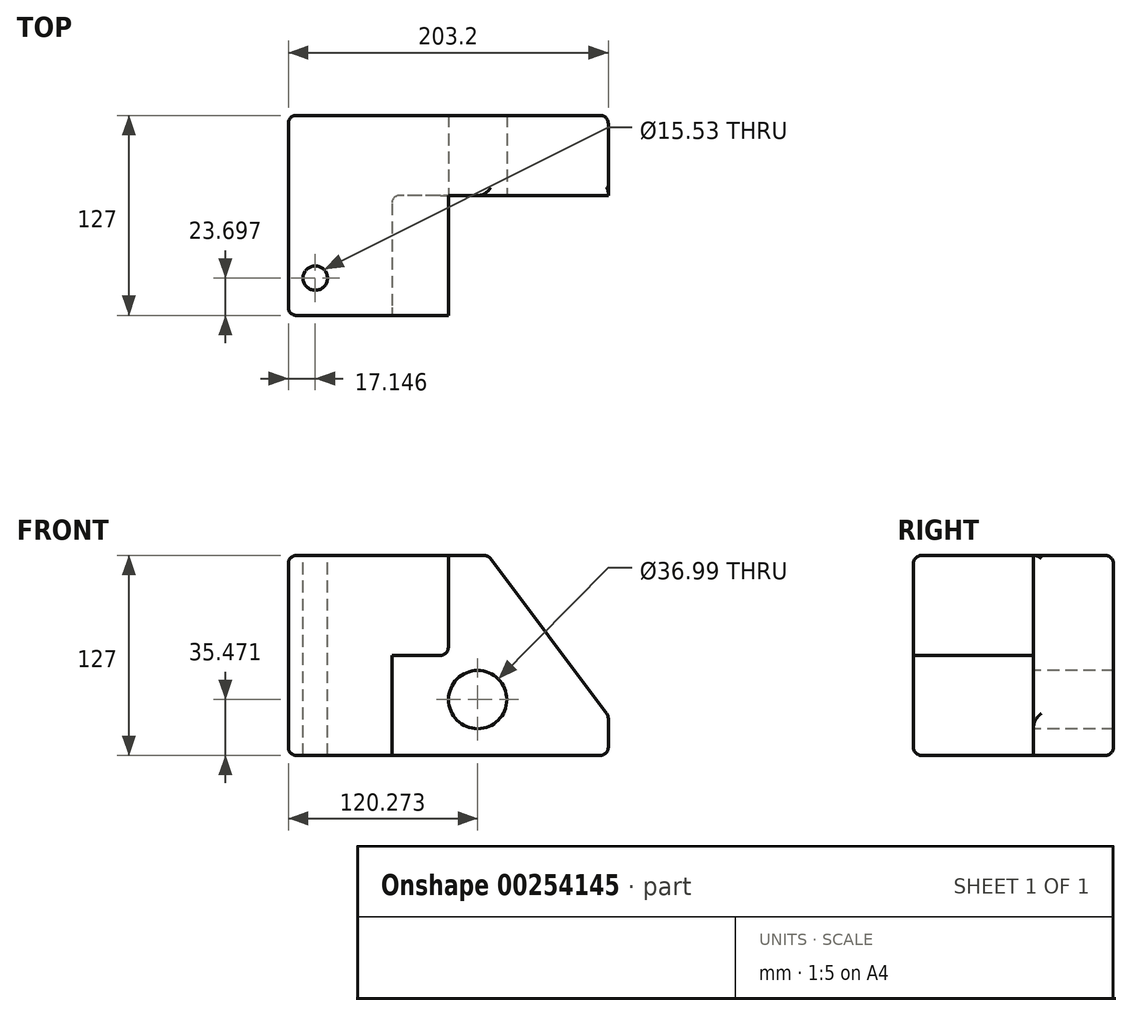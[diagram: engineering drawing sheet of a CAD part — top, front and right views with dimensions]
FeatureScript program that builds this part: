
annotation { "Feature Type Name" : "Feature", "Feature Type Description" : "" }
export const myFeature = defineFeature(function(context is Context, id is Id, definition is map)
    precondition{}
    {
        {
            var Q0;
            Q0=qCreatedBy(makeId("Front.planeOp"),FACE);
            var sketch = newSketch(context, id + "F0", { "sketchPlane" : qUnion([Q0])});
            skLineSegment(sketch, "E0.bottom", {"start": v(101.6, -63.5) * mm, "end": v(-101.6, -63.5) * mm});
            skLineSegment(sketch, "E0.top", {"start": v(101.6, 63.5) * mm, "end": v(-101.6, 63.5) * mm});
            skLineSegment(sketch, "E0.left", {"start": v(101.6, -63.5) * mm, "end": v(101.6, 63.5) * mm});
            skLineSegment(sketch, "E0.right", {"start": v(-101.6, -63.5) * mm, "end": v(-101.6, 63.5) * mm});
            skPoint(sketch, "E0.middle", {"position": v(0, 0) * mm});
            skSolve(sketch);
        }
        {
            var Q0;
            Q0=makeQuery(id+"F0.imprint","IMPRINT",FACE,{"disambiguationData":[TD([[makeQuery(id+"F0.imprint","IMPRINT",EDGE,{"derivedFrom":sQuery(id+"F0.wireOp",EDGE,"E0.bottom")}),-1.0]])]});
            extrude(context, id + "F1", {"entities" : qUnion([Q0]), "depth" : 127 * mm});
        }
        {
            var Q0;
            Q0=makeQuery(id+"F1.opExtrude","CAP_FACE",FACE,{"disambiguationData":[OSD([sQuery(id+"F0.wireOp",EDGE,"E0.bottom"),sQuery(id+"F0.wireOp",EDGE,"E0.top"),sQuery(id+"F0.wireOp",EDGE,"E0.left"),sQuery(id+"F0.wireOp",EDGE,"E0.right")])],"isStart":false});
            var sketch = newSketch(context, id + "F2", { "sketchPlane" : qUnion([Q0])});
            skLineSegment(sketch, "E1", {"start": v(0, 63.5) * mm, "end": v(0, 0) * mm});
            skLineSegment(sketch, "E2", {"start": v(0, 0) * mm, "end": v(-35.84, 0) * mm});
            skLineSegment(sketch, "E3", {"start": v(-35.84, 0) * mm, "end": v(-35.84, -63.5) * mm});
            skSolve(sketch);
        }
        {
            var Q0;
            {var subQ2=sQuery(id+"F2.wireOp",EDGE,"E1");Q0=makeQuery(id+"F2.imprint","IMPRINT",FACE,{"disambiguationData":[TD([[makeQuery(id+"F2.imprint","IMPRINT",EDGE,{"derivedFrom":subQ2}),1.0]])]});}
            extrude(context, id + "F3", {"entities" : qUnion([Q0]), "operationType" : NewBodyOperationType.REMOVE, "oppositeDirection" : true, "depth" : 76.2 * mm});
        }
        {
            var Q0;
            Q0=makeQuery(id+"F1.opExtrude","SWEPT_EDGE",EDGE,{"disambiguationData":[OSD([sQuery(id+"F0.wireOp",EDGE,"E0.top"),sQuery(id+"F0.wireOp",EDGE,"E0.left")])]});
            chamfer(context, id + "F4", {"entities" : qUnion([Q0]), "chamferType" : ChamferType.TWO_OFFSETS, "width1" : 76.2 * mm, "oppositeDirection" : false, "width2" : 101.6 * mm, "tangentPropagation" : true});
        }
        {
            var Q0;
            Q0=makeQuery(id+"F1.opExtrude","SWEPT_EDGE",EDGE,{"disambiguationData":[OSD([sQuery(id+"F0.wireOp",EDGE,"E0.top"),sQuery(id+"F0.wireOp",EDGE,"E0.right")])]});
            var Q1;
            Q1=makeQuery(id+"F1.opExtrude","CAP_EDGE",EDGE,{"disambiguationData":[OSD([sQuery(id+"F0.wireOp",EDGE,"E0.top")])],"isStart":false});
            var Q2;
            Q2=makeQuery(id+"F3.boolean.opBoolean","COPY",EDGE,{"derivedFrom":makeQuery(id+"F3.opExtrude","SWEPT_EDGE",EDGE,{"disambiguationData":[OSD([sQuery(id+"F0.wireOp",EDGE,"E0.top"),sQuery(id+"F2.wireOp",EDGE,"E1")])]})});
            var Q3;
            Q3=makeQuery(id+"F3.boolean.opBoolean","COPY",EDGE,{"derivedFrom":makeQuery(id+"F3.opExtrude","CAP_EDGE",EDGE,{"disambiguationData":[OSD([sQuery(id+"F0.wireOp",EDGE,"E0.top")])],"isStart":false})});
            var Q4;
            {var subQ0=sQuery(id+"F0.wireOp",EDGE,"E0.top");Q4=makeQuery(id+"F4.opChamfer","BLEND_EDGE",EDGE,{"blendedFrom":[makeQuery(id+"F1.opExtrude","SWEPT_EDGE",EDGE,{"disambiguationData":[OSD([subQ0,sQuery(id+"F0.wireOp",EDGE,"E0.left")])]}),makeQuery(id+"F1.opExtrude","SWEPT_FACE",FACE,{"disambiguationData":[OSD([subQ0])]})],"blendedInto":[makeQuery(id+"F1.opExtrude","SWEPT_FACE",FACE,{"disambiguationData":[OSD([subQ0])]})]});}
            var Q5;
            Q5=makeQuery(id+"F1.opExtrude","CAP_EDGE",EDGE,{"disambiguationData":[OSD([sQuery(id+"F0.wireOp",EDGE,"E0.top")])],"isStart":true});
            var Q6;
            Q6=makeQuery(id+"F3.boolean.opBoolean","COPY",EDGE,{"derivedFrom":makeQuery(id+"F3.opExtrude","CAP_EDGE",EDGE,{"disambiguationData":[OSD([sQuery(id+"F2.wireOp",EDGE,"E2")])],"isStart":true})});
            var Q7;
            Q7=makeQuery(id+"F3.boolean.opBoolean","COPY",EDGE,{"derivedFrom":makeQuery(id+"F3.opExtrude","SWEPT_EDGE",EDGE,{"disambiguationData":[OSD([sQuery(id+"F2.wireOp",EDGE,"E1"),sQuery(id+"F2.wireOp",EDGE,"E2")])]})});
            var Q8;
            Q8=makeQuery(id+"F1.opExtrude","CAP_EDGE",EDGE,{"disambiguationData":[OSD([sQuery(id+"F0.wireOp",EDGE,"E0.right")])],"isStart":false});
            var Q9;
            Q9=makeQuery(id+"F1.opExtrude","CAP_EDGE",EDGE,{"disambiguationData":[OSD([sQuery(id+"F0.wireOp",EDGE,"E0.bottom")])],"isStart":false});
            var Q10;
            Q10=makeQuery(id+"F3.boolean.opBoolean","COPY",EDGE,{"derivedFrom":makeQuery(id+"F3.opExtrude","SWEPT_EDGE",EDGE,{"disambiguationData":[OSD([sQuery(id+"F0.wireOp",EDGE,"E0.bottom"),sQuery(id+"F2.wireOp",EDGE,"E3")])]})});
            var Q11;
            Q11=makeQuery(id+"F3.boolean.opBoolean","COPY",EDGE,{"derivedFrom":makeQuery(id+"F3.opExtrude","CAP_EDGE",EDGE,{"disambiguationData":[OSD([sQuery(id+"F2.wireOp",EDGE,"E3")])],"isStart":false})});
            var Q12;
            Q12=makeQuery(id+"F3.boolean.opBoolean","COPY",EDGE,{"derivedFrom":makeQuery(id+"F3.opExtrude","CAP_EDGE",EDGE,{"disambiguationData":[OSD([sQuery(id+"F0.wireOp",EDGE,"E0.bottom")])],"isStart":false})});
            var Q13;
            Q13=makeQuery(id+"F3.boolean.opBoolean","COPY",EDGE,{"derivedFrom":makeQuery(id+"F3.opExtrude","CAP_EDGE",EDGE,{"disambiguationData":[OSD([sQuery(id+"F0.wireOp",EDGE,"E0.left")])],"isStart":false})});
            var Q14;
            Q14=makeQuery(id+"F1.opExtrude","SWEPT_EDGE",EDGE,{"disambiguationData":[OSD([sQuery(id+"F0.wireOp",EDGE,"E0.bottom"),sQuery(id+"F0.wireOp",EDGE,"E0.left")])]});
            var Q15;
            Q15=makeQuery(id+"F1.opExtrude","CAP_EDGE",EDGE,{"disambiguationData":[OSD([sQuery(id+"F0.wireOp",EDGE,"E0.left")])],"isStart":true});
            var Q16;
            {var subQ0=sQuery(id+"F0.wireOp",EDGE,"E0.left");Q16=makeQuery(id+"F4.opChamfer","BLEND_EDGE",EDGE,{"blendedFrom":[makeQuery(id+"F1.opExtrude","SWEPT_EDGE",EDGE,{"disambiguationData":[OSD([sQuery(id+"F0.wireOp",EDGE,"E0.top"),subQ0])]}),makeQuery(id+"F1.opExtrude","SWEPT_FACE",FACE,{"disambiguationData":[OSD([subQ0])]})],"blendedInto":[makeQuery(id+"F1.opExtrude","SWEPT_FACE",FACE,{"disambiguationData":[OSD([subQ0])]})]});}
            var Q17;
            {var subQ0=sQuery(id+"F0.wireOp",EDGE,"E0.left");var subQ1=sQuery(id+"F0.wireOp",EDGE,"E0.top");Q17=makeQuery(id+"F4.opChamfer","BLEND_EDGE",EDGE,{"blendedFrom":[makeQuery(id+"F1.opExtrude","SWEPT_EDGE",EDGE,{"disambiguationData":[OSD([subQ1,subQ0])]}),makeQuery(id+"F3.boolean.opBoolean","COPY",FACE,{"derivedFrom":makeQuery(id+"F3.opExtrude","CAP_FACE",FACE,{"disambiguationData":[OSD([sQuery(id+"F0.wireOp",EDGE,"E0.bottom"),subQ1,subQ0,sQuery(id+"F2.wireOp",EDGE,"E1"),sQuery(id+"F2.wireOp",EDGE,"E2"),sQuery(id+"F2.wireOp",EDGE,"E3")])],"isStart":false})})],"blendedInto":[makeQuery(id+"F3.boolean.opBoolean","COPY",FACE,{"derivedFrom":makeQuery(id+"F3.opExtrude","CAP_FACE",FACE,{"disambiguationData":[OSD([sQuery(id+"F0.wireOp",EDGE,"E0.bottom"),subQ1,subQ0,sQuery(id+"F2.wireOp",EDGE,"E1"),sQuery(id+"F2.wireOp",EDGE,"E2"),sQuery(id+"F2.wireOp",EDGE,"E3")])],"isStart":false})})]});}
            var Q18;
            {var subQ0=sQuery(id+"F0.wireOp",EDGE,"E0.left");var subQ1=sQuery(id+"F0.wireOp",EDGE,"E0.top");Q18=makeQuery(id+"F4.opChamfer","BLEND_EDGE",EDGE,{"blendedFrom":[makeQuery(id+"F1.opExtrude","SWEPT_EDGE",EDGE,{"disambiguationData":[OSD([subQ1,subQ0])]}),makeQuery(id+"F1.opExtrude","CAP_FACE",FACE,{"disambiguationData":[OSD([sQuery(id+"F0.wireOp",EDGE,"E0.bottom"),subQ1,subQ0,sQuery(id+"F0.wireOp",EDGE,"E0.right")])],"isStart":true})],"blendedInto":[makeQuery(id+"F1.opExtrude","CAP_FACE",FACE,{"disambiguationData":[OSD([sQuery(id+"F0.wireOp",EDGE,"E0.bottom"),subQ1,subQ0,sQuery(id+"F0.wireOp",EDGE,"E0.right")])],"isStart":true})]});}
            fillet(context, id + "F5", {"entities" : qUnion([Q0, Q1, Q2, Q3, Q4, Q5, Q6, Q7, Q8, Q9, Q10, Q11, Q12, Q13, Q14, Q15, Q16, Q17, Q18]), "radius" : 5.08 * mm, "tangentPropagation" : true, "allowEdgeOverflow" : false});
        }
        {
            var Q0;
            Q0=makeQuery(id+"F1.opExtrude","SWEPT_EDGE",EDGE,{"disambiguationData":[OSD([sQuery(id+"F0.wireOp",EDGE,"E0.bottom"),sQuery(id+"F0.wireOp",EDGE,"E0.right")])]});
            var Q1;
            Q1=makeQuery(id+"F1.opExtrude","CAP_EDGE",EDGE,{"disambiguationData":[OSD([sQuery(id+"F0.wireOp",EDGE,"E0.right")])],"isStart":true});
            var Q2;
            Q2=makeQuery(id+"F1.opExtrude","CAP_EDGE",EDGE,{"disambiguationData":[OSD([sQuery(id+"F0.wireOp",EDGE,"E0.bottom")])],"isStart":true});
            fillet(context, id + "F6", {"entities" : qUnion([Q0, Q1, Q2]), "radius" : 5.08 * mm, "tangentPropagation" : true, "allowEdgeOverflow" : false});
        }
        {
            var Q0;
            Q0=makeQuery(id+"F3.boolean.opBoolean","COPY",FACE,{"derivedFrom":makeQuery(id+"F3.opExtrude","CAP_FACE",FACE,{"disambiguationData":[OSD([sQuery(id+"F0.wireOp",EDGE,"E0.bottom"),sQuery(id+"F0.wireOp",EDGE,"E0.top"),sQuery(id+"F0.wireOp",EDGE,"E0.left"),sQuery(id+"F2.wireOp",EDGE,"E1"),sQuery(id+"F2.wireOp",EDGE,"E2"),sQuery(id+"F2.wireOp",EDGE,"E3")])],"isStart":false})});
            var sketch = newSketch(context, id + "F7", { "sketchPlane" : qUnion([Q0])});
            skCircle(sketch, "E4", {"center": v(18.67, -28.03) * mm, "radius": 18.5 * mm});
            skSolve(sketch);
        }
        {
            var Q0;
            Q0=makeQuery(id+"F7.imprint","IMPRINT",FACE,{"disambiguationData":[TD([[makeQuery(id+"F7.imprint","IMPRINT",EDGE,{"derivedFrom":sQuery(id+"F7.wireOp",EDGE,"E4")}),1.0]])]});
            var Q1;
            Q1=makeQuery(id+"F1.opExtrude","CAP_FACE",FACE,{"disambiguationData":[OSD([sQuery(id+"F0.wireOp",EDGE,"E0.bottom"),sQuery(id+"F0.wireOp",EDGE,"E0.top"),sQuery(id+"F0.wireOp",EDGE,"E0.left"),sQuery(id+"F0.wireOp",EDGE,"E0.right")])],"isStart":true});
            extrude(context, id + "F8", {"entities" : qUnion([Q0]), "operationType" : NewBodyOperationType.REMOVE, "endBound" : BoundingType.UP_TO_SURFACE, "oppositeDirection" : true, "endBoundEntityFace" : qUnion([Q1]), "depth" : 25.4 * mm});
        }
        {
            var Q0;
            Q0=makeQuery(id+"F1.opExtrude","SWEPT_FACE",FACE,{"disambiguationData":[OSD([sQuery(id+"F0.wireOp",EDGE,"E0.top")])]});
            var sketch = newSketch(context, id + "F9", { "sketchPlane" : qUnion([Q0])});
            skCircle(sketch, "E5", {"center": v(-84.45, -103.3) * mm, "radius": 7.77 * mm});
            skSolve(sketch);
        }
        {
            var Q0;
            Q0=makeQuery(id+"F9.imprint","IMPRINT",FACE,{"disambiguationData":[TD([[makeQuery(id+"F9.imprint","IMPRINT",EDGE,{"derivedFrom":sQuery(id+"F9.wireOp",EDGE,"E5")}),1.0]])]});
            var Q1;
            Q1=sQuery(id+"F9.wireOp",EDGE,"E5");
            var Q2;
            Q2=makeQuery(id+"F1.opExtrude","SWEPT_FACE",FACE,{"disambiguationData":[OSD([sQuery(id+"F0.wireOp",EDGE,"E0.bottom")])]});
            extrude(context, id + "F10", {"entities" : qUnion([Q0]), "operationType" : NewBodyOperationType.REMOVE, "surfaceEntities" : qUnion([Q1]), "endBound" : BoundingType.UP_TO_SURFACE, "oppositeDirection" : true, "endBoundEntityFace" : qUnion([Q2]), "depth" : 25.4 * mm});
        }
    });
